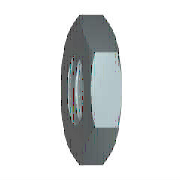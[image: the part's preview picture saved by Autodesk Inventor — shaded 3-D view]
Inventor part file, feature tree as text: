
AUTODESK INVENTOR PART (.ipt)
format: ipt  version: 2011 SP1 (Build 150282100, 282)  size: 164,864 bytes
history: native  units: mm (DEFAULTED — no unit token found)
features: sketch x4, other x3, revolve x1
ambient origin geometry x8: Origin, YZ Plane, XZ Plane, XY Plane, X Axis, Y Axis, Z Axis, Center Point
bodies: Solid1 (feature_tree)
feature tree (8):
  revolve  "Revolution2"  [1 undecoded]
  other  "MSC_PF1"
  other  "MSC_PT1"
  other  "MSC_A1"
  sketch  "Sketch7"  dims[d1=1.6875mm d13=1.6875mm]
  sketch  "Sketch9"  dims[d17=1.125mm]
  sketch  "Sketch10"  dims[d21=30.0deg]
  sketch  "Sketch11"  dims[d23=0.0mm d24=0.0mm d25=0.0mm d26=0.0mm d29=3.302mm d30=0.0mm d38=9.525mm d40=9.525mm d41=150.0deg d42=90.0deg d45=9.525mm d46=150.0deg d47=90.0deg d50=0.0mm d51=0.0mm d56=3.9624mm d57=12.7mm d58=9.525mm d59=6.35mm d60=14.3117mm d61=19.05mm d62=20.594885mm d63=0.015625mm d64=3.175mm d65=45.0deg d67=0.0mm d69=0.0mm d70=0.0mm d72=0.0mm]
note: 1 required parameter value undecoded (feature->parameter linkage not recoverable at this tier; creation-order binding heuristic only, values carry confidence <= 0.55)
